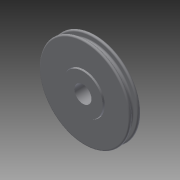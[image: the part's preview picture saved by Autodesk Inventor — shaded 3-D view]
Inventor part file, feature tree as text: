
AUTODESK INVENTOR PART (.ipt)
format: ipt  version: 2015 SP1 (Build 190203100, 203)  size: 151,040 bytes
history: native  units: in
note: dims shown in document units (in); Inventor stores cm internally (conversion verified against a paired STEP export)
features: extrude x4, sketch x4, plane x1, fillet x1
ambient origin geometry x8: Origin, YZ Plane, XZ Plane, XY Plane, X Axis, Y Axis, Z Axis, Center Point
bodies: Solid1 (feature_tree)
feature tree (10):
  extrude  "Extrusion1"  Depth=2.0in
  plane  "Work Plane1"
  extrude  "Extrusion2"  Depth=0.25in
  fillet  "Fillet1"  Radius=1.75in
  extrude  "Extrusion3"  Depth=0.0312in
  extrude  "Extrusion4"  Depth=0.3125in TaperAngle=0.0deg
  sketch  "Sketch1"  dims[d0=0.9in d1=2.0in]
  sketch  "Sketch2"  dims[d2=0.25in d3=0.0in d4=2.0in d5=1.75in]
  sketch  "Sketch3"  dims[d6=0.125in d7=0.0in d8=0.0312in]
  sketch  "Sketch4"  dims[d9=0.875in d10=0.3125in d11=0.0in d12=0.375in d13=1.0in d14=0.0in]
